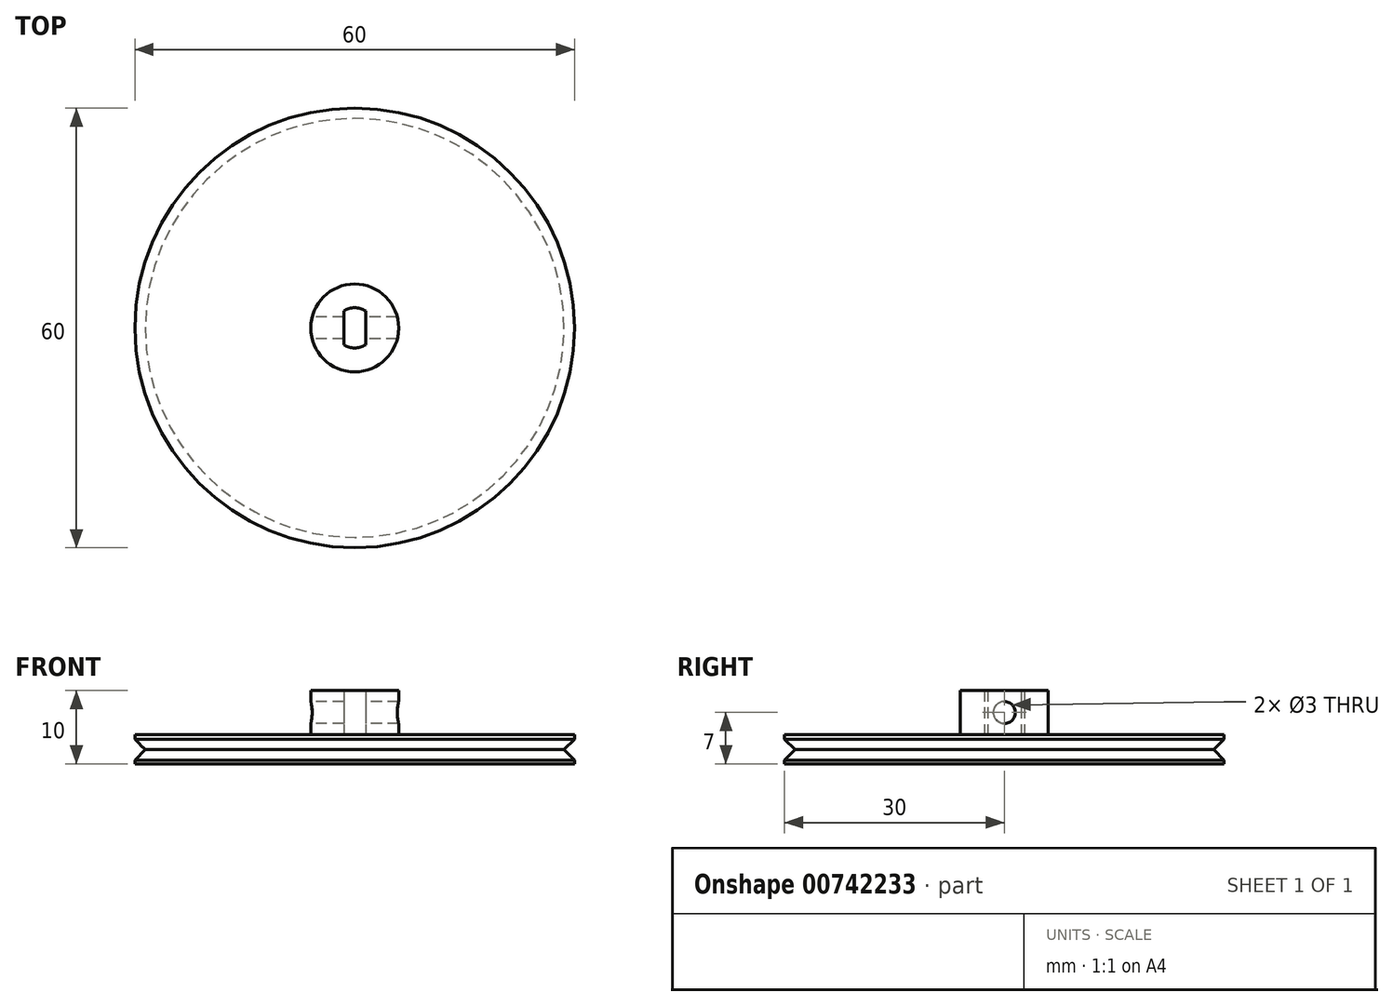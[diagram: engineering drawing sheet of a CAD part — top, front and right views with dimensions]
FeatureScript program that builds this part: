
annotation { "Feature Type Name" : "Feature", "Feature Type Description" : "" }
export const myFeature = defineFeature(function(context is Context, id is Id, definition is map)
    precondition{}
    {
        {
            var Q0;
            Q0=qCreatedBy(makeId("Top.planeOp"),FACE);
            var sketch = newSketch(context, id + "F0", { "sketchPlane" : qUnion([Q0])});
            skCircle(sketch, "E0", {"center": v(0, 0) * mm, "radius": 30 * mm});
            skSolve(sketch);
        }
        {
            var Q0;
            Q0=makeQuery(id+"F0.imprint","IMPRINT",FACE,{"disambiguationData":[TD([[makeQuery(id+"F0.imprint","IMPRINT",EDGE,{"derivedFrom":sQuery(id+"F0.wireOp",EDGE,"E0")}),1.0]])]});
            extrude(context, id + "F1", {"entities" : qUnion([Q0]), "depth" : 4 * mm, "offsetDistance" : 25 * mm});
        }
        {
            var Q0;
            Q0=makeQuery(id+"F1.opExtrude","CAP_FACE",FACE,{"disambiguationData":[OSD([sQuery(id+"F0.wireOp",EDGE,"E0")])],"isStart":false});
            var sketch = newSketch(context, id + "F2", { "sketchPlane" : qUnion([Q0])});
            skCircle(sketch, "E1", {"center": v(0, 0) * mm, "radius": 6 * mm});
            skLineSegment(sketch, "E2.bottom", {"start": v(1.5, -2.3) * mm, "end": v(-1.5, -2.3) * mm});
            skLineSegment(sketch, "E2.top", {"start": v(1.5, 2.3) * mm, "end": v(-1.5, 2.3) * mm});
            skLineSegment(sketch, "E2.left", {"start": v(1.5, -2.3) * mm, "end": v(1.5, 2.3) * mm});
            skLineSegment(sketch, "E2.right", {"start": v(-1.5, -2.3) * mm, "end": v(-1.5, 2.3) * mm});
            skArc(sketch, "E3", {"start": v(1.5, 2.3) * mm, "mid": v(0, 2.75) * mm, "end": v(-1.5, 2.3) * mm});
            skArc(sketch, "E4", {"start": v(-1.5, -2.3) * mm, "mid": v(0, -2.75) * mm, "end": v(1.5, -2.3) * mm});
            skSolve(sketch);
        }
        {
            var Q0;
            Q0=makeQuery(id+"F2.imprint","IMPRINT",FACE,{"disambiguationData":[TD([[makeQuery(id+"F2.imprint","IMPRINT",EDGE,{"derivedFrom":sQuery(id+"F2.wireOp",EDGE,"E1")}),1.0]])]});
            extrude(context, id + "F3", {"entities" : qUnion([Q0]), "operationType" : NewBodyOperationType.ADD, "depth" : 6 * mm, "offsetDistance" : 25 * mm});
        }
        {
            var Q0;
            Q0=qCreatedBy(makeId("Right.planeOp"),FACE);
            var sketch = newSketch(context, id + "F4", { "sketchPlane" : qUnion([Q0])});
            skCircle(sketch, "E5", {"center": v(0, 7) * mm, "radius": 1.5 * mm});
            skSolve(sketch);
        }
        {
            var Q0;
            Q0=qSketchRegion(id+"F4",true);
            extrude(context, id + "F5", {"entities" : qUnion([Q0]), "operationType" : NewBodyOperationType.REMOVE, "endBound" : BoundingType.SYMMETRIC, "depth" : 24.6 * mm, "offsetDistance" : 25 * mm});
        }
        {
            var Q0;
            Q0=qCreatedBy(makeId("Front.planeOp"),FACE);
            var sketch = newSketch(context, id + "F6", { "sketchPlane" : qUnion([Q0])});
            skLineSegment(sketch, "E6", {"start": v(-30, 0) * mm, "end": v(-30, 4) * mm});
            skLineSegment(sketch, "E7", {"start": v(-30, 3.34) * mm, "end": v(-28.59, 1.93) * mm});
            skLineSegment(sketch, "E8", {"start": v(-28.59, 1.93) * mm, "end": v(-30, 0.51) * mm});
            skLineSegment(sketch, "E9", {"start": v(0, 22.53) * mm, "end": v(0, -10.3) * mm, "construction": true});
            skSolve(sketch);
        }
        {
            var Q0;
            Q0=qSketchRegion(id+"F6",true);
            var Q1;
            Q1=sQuery(id+"F6.wireOp",EDGE,"E9");
            revolve(context, id + "F7", {"operationType" : NewBodyOperationType.REMOVE, "surfaceOperationType" : NewSurfaceOperationType.NEW, "entities" : qUnion([Q0]), "axis" : qUnion([Q1]), "revolveType" : RevolveType.FULL, "oppositeDirection" : true});
        }
    });
